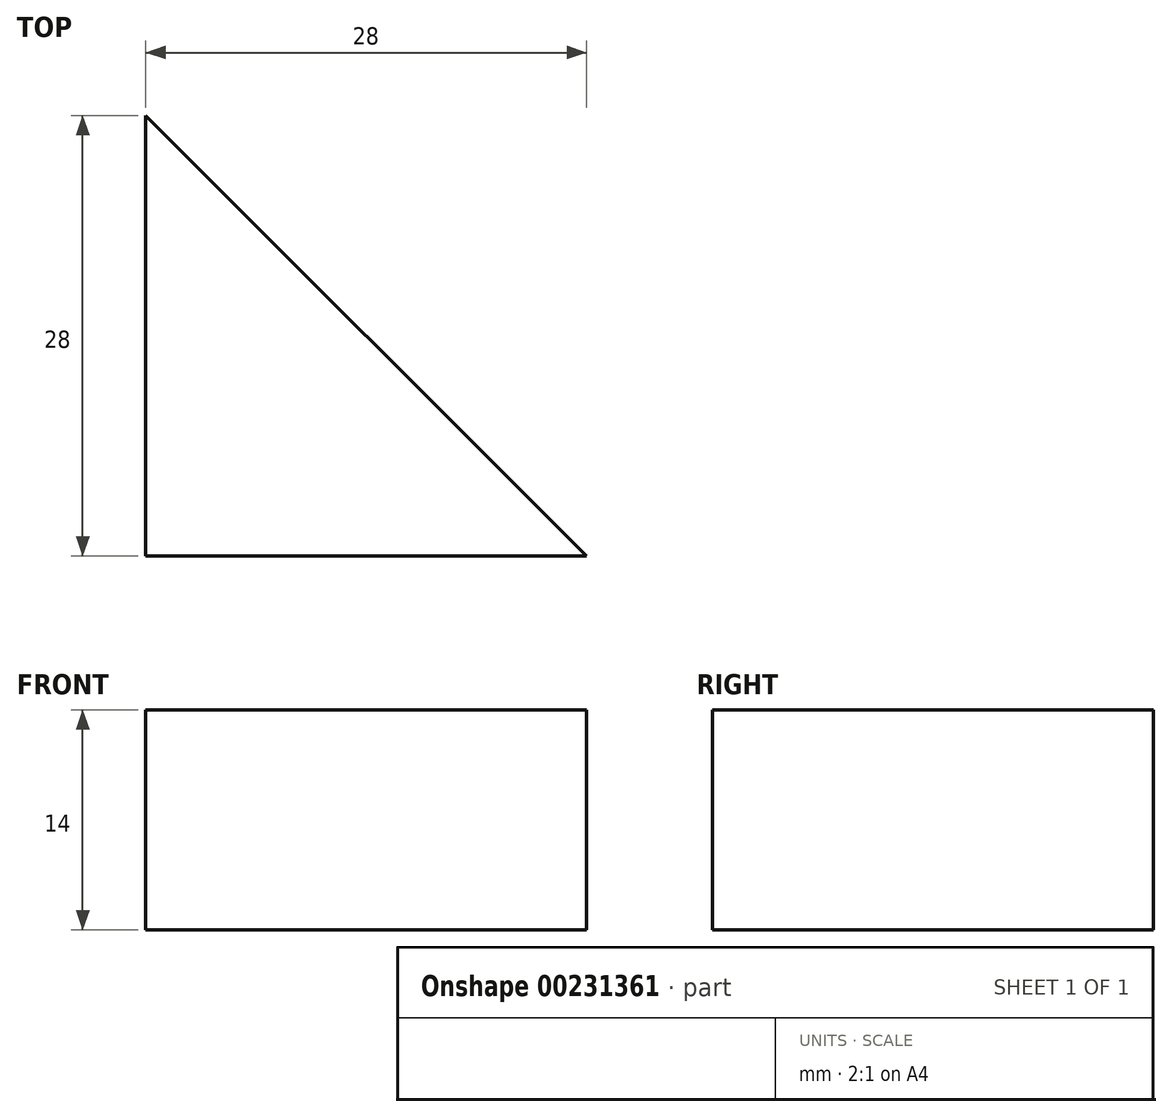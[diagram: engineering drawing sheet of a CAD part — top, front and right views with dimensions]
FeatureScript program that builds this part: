
annotation { "Feature Type Name" : "Feature", "Feature Type Description" : "" }
export const myFeature = defineFeature(function(context is Context, id is Id, definition is map)
    precondition{}
    {
        {
            var Q0;
            Q0=qCreatedBy(makeId("Top.planeOp"),FACE);
            var sketch = newSketch(context, id + "F0", { "sketchPlane" : qUnion([Q0])});
            skLineSegment(sketch, "E0", {"start": v(0, 0) * mm, "end": v(14, 0) * mm});
            skLineSegment(sketch, "E1", {"start": v(14, 0) * mm, "end": v(0, 14) * mm});
            skLineSegment(sketch, "E2", {"start": v(0, 14) * mm, "end": v(0, 0) * mm});
            skLineSegment(sketch, "E3", {"start": v(0, 14) * mm, "end": v(-14, 28) * mm});
            skLineSegment(sketch, "E4", {"start": v(-14, 28) * mm, "end": v(-14, 0) * mm});
            skLineSegment(sketch, "E5", {"start": v(-14, 0) * mm, "end": v(0, 0) * mm});
            skSolve(sketch);
        }
        {
            var Q0;
            Q0 = qSketchRegion(id + "F0", true);
            extrude(context, id + "F1", {"entities" : qUnion([Q0]), "depth" : 14 * mm});
        }
    });
